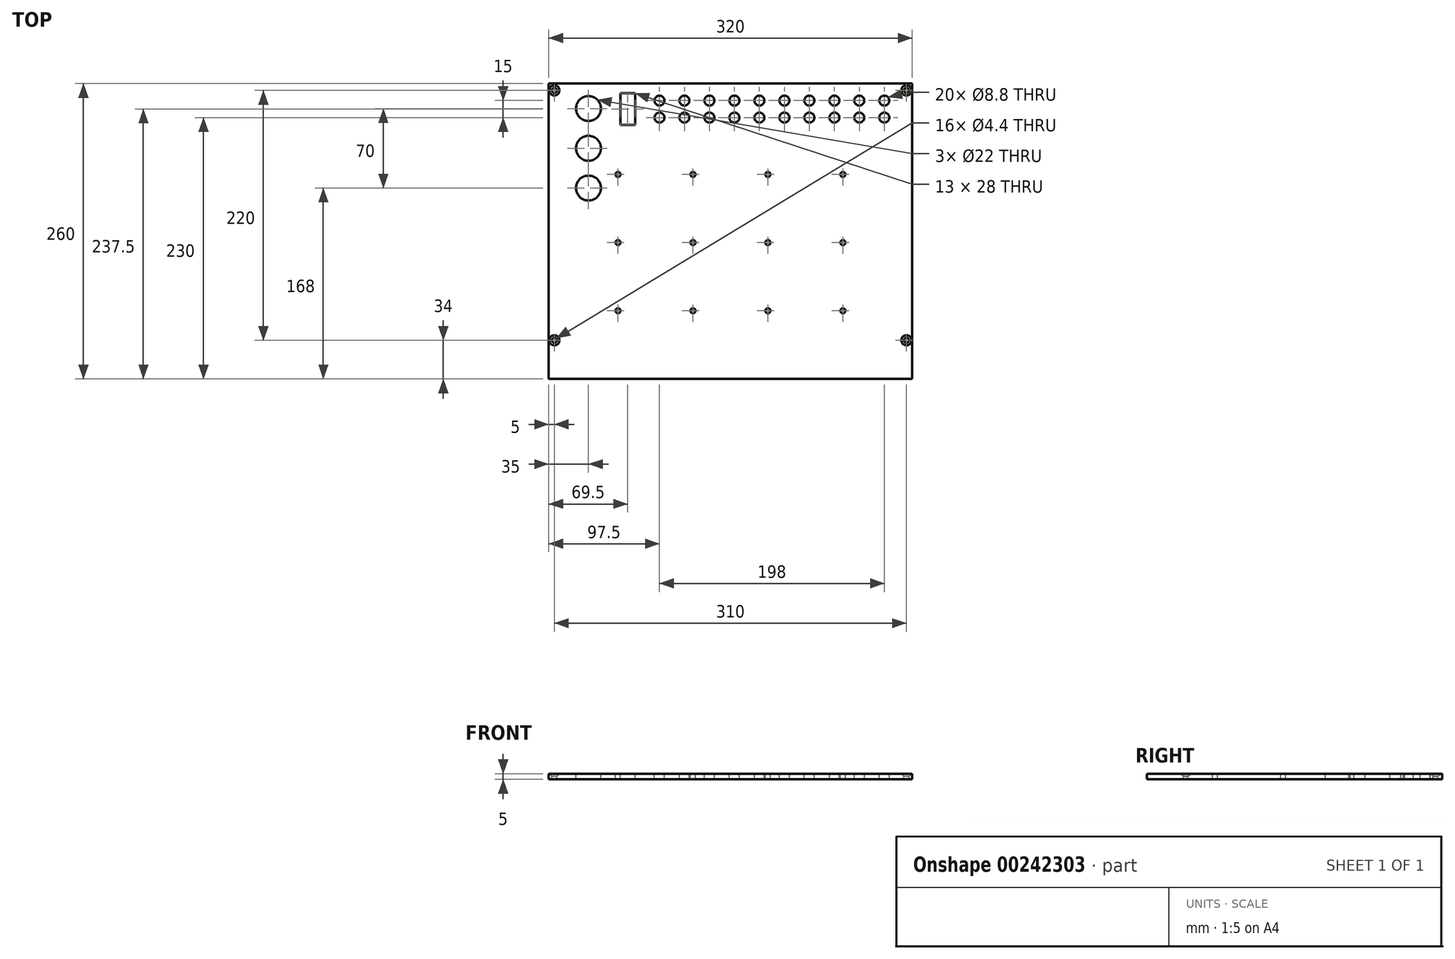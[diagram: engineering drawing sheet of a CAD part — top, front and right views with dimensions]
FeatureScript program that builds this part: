
annotation { "Feature Type Name" : "Feature", "Feature Type Description" : "" }
export const myFeature = defineFeature(function(context is Context, id is Id, definition is map)
    precondition{}
    {
        {
            var Q0;
            Q0=qCreatedBy(makeId("Top.planeOp"),FACE);
            var sketch = newSketch(context, id + "F0", { "sketchPlane" : qUnion([Q0])});
            skLineSegment(sketch, "E0.bottom", {"start": v(160, -130) * mm, "end": v(-160, -130) * mm});
            skLineSegment(sketch, "E0.top", {"start": v(160, 130) * mm, "end": v(-160, 130) * mm});
            skLineSegment(sketch, "E0.left", {"start": v(160, -130) * mm, "end": v(160, 130) * mm});
            skLineSegment(sketch, "E0.right", {"start": v(-160, -130) * mm, "end": v(-160, 130) * mm});
            skPoint(sketch, "E0.middle", {"position": v(0, 0) * mm});
            skSolve(sketch);
        }
        {
            var Q0;
            Q0=qSketchRegion(id+"F0",true);
            extrude(context, id + "F1", {"entities" : qUnion([Q0]), "endBound" : BoundingType.SYMMETRIC, "depth" : 5 * mm});
        }
        {
            var Q0;
            Q0=makeQuery(id+"F1.opExtrude","CAP_FACE",FACE,{"disambiguationData":[OSD([sQuery(id+"F0.wireOp",EDGE,"E0.bottom"),sQuery(id+"F0.wireOp",EDGE,"E0.top"),sQuery(id+"F0.wireOp",EDGE,"E0.left"),sQuery(id+"F0.wireOp",EDGE,"E0.right")])],"isStart":false});
            var sketch = newSketch(context, id + "F2", { "sketchPlane" : qUnion([Q0])});
            skCircle(sketch, "E1", {"center": v(-155, -96) * mm, "radius": 2 * mm});
            skCircle(sketch, "E2.0.1.0", {"center": v(-155, 124) * mm, "radius": 2 * mm});
            skCircle(sketch, "E2.1.0.0", {"center": v(155, -96) * mm, "radius": 2 * mm});
            skCircle(sketch, "E2.1.1.0", {"center": v(155, 124) * mm, "radius": 2 * mm});
            skLineSegment(sketch, "E2.direction1", {"start": v(-155, -96) * mm, "end": v(155, -96) * mm, "construction": true});
            skLineSegment(sketch, "E2.direction2", {"start": v(-155, -96) * mm, "end": v(-155, 124) * mm, "construction": true});
            skSolve(sketch);
        }
        {
            var Q0;
            Q0=sQuery(id+"F2.wireOp",VERTEX,"E1.center");
            var Q1;
            Q1=sQuery(id+"F2.wireOp",VERTEX,"E2.0.1.0.center");
            var Q2;
            Q2=sQuery(id+"F2.wireOp",VERTEX,"E2.1.1.0.center");
            var Q3;
            Q3=sQuery(id+"F2.wireOp",VERTEX,"E2.1.0.0.center");
            var Q4;
            Q4=makeQuery(id+"F1.opExtrude","SWEPT_BODY",BODY,{"disambiguationData":[OSD([sQuery(id+"F0.wireOp",EDGE,"E0.bottom"),sQuery(id+"F0.wireOp",EDGE,"E0.top"),sQuery(id+"F0.wireOp",EDGE,"E0.left"),sQuery(id+"F0.wireOp",EDGE,"E0.right")])]});
            hole(context, id + "F3", {"style" : HoleStyle.C_SINK, "endStyle" : HoleEndStyle.BLIND, "standardTappedOrClearance" : lookupTablePath({ "standard" : "ISO", "fit" : "Normal", "size" : "M4", "type" : "Clearance" }), "standardBlindInLast" : lookupTablePath({ "fit" : "Standard", "standard" : "ISO", "size" : "M4", "type" : "Clearance" }), "holeDiameter" : 4.4 * mm, "cSinkDiameter" : 8.96 * mm, "cSinkAngle" : 90 * degree, "holeDepth" : 17.25 * mm, "tappedDepth" : 15 * mm, "tapClearance" : 3, "locations" : qUnion([Q0, Q1, Q2, Q3]), "scope" : qUnion([Q4])});
        }
        {
            var Q0;
            Q0=makeQuery(id+"F1.opExtrude","CAP_FACE",FACE,{"disambiguationData":[OSD([sQuery(id+"F0.wireOp",EDGE,"E0.bottom"),sQuery(id+"F0.wireOp",EDGE,"E0.top"),sQuery(id+"F0.wireOp",EDGE,"E0.left"),sQuery(id+"F0.wireOp",EDGE,"E0.right")])],"isStart":false});
            var sketch = newSketch(context, id + "F4", { "sketchPlane" : qUnion([Q0])});
            skCircle(sketch, "E3", {"center": v(-62.5, 115) * mm, "radius": 4 * mm});
            skCircle(sketch, "E4.0.1.0", {"center": v(-62.5, 100) * mm, "radius": 4 * mm});
            skCircle(sketch, "E4.1.0.0", {"center": v(-40.5, 115) * mm, "radius": 4 * mm});
            skCircle(sketch, "E4.1.1.0", {"center": v(-40.5, 100) * mm, "radius": 4 * mm});
            skCircle(sketch, "E4.2.0.0", {"center": v(-18.5, 115) * mm, "radius": 4 * mm});
            skCircle(sketch, "E4.2.1.0", {"center": v(-18.5, 100) * mm, "radius": 4 * mm});
            skCircle(sketch, "E4.3.0.0", {"center": v(3.5, 115) * mm, "radius": 4 * mm});
            skCircle(sketch, "E4.3.1.0", {"center": v(3.5, 100) * mm, "radius": 4 * mm});
            skCircle(sketch, "E4.4.0.0", {"center": v(25.5, 115) * mm, "radius": 4 * mm});
            skCircle(sketch, "E4.4.1.0", {"center": v(25.5, 100) * mm, "radius": 4 * mm});
            skCircle(sketch, "E4.5.0.0", {"center": v(47.5, 115) * mm, "radius": 4 * mm});
            skCircle(sketch, "E4.5.1.0", {"center": v(47.5, 100) * mm, "radius": 4 * mm});
            skCircle(sketch, "E4.6.0.0", {"center": v(69.5, 115) * mm, "radius": 4 * mm});
            skCircle(sketch, "E4.6.1.0", {"center": v(69.5, 100) * mm, "radius": 4 * mm});
            skCircle(sketch, "E4.7.0.0", {"center": v(91.5, 115) * mm, "radius": 4 * mm});
            skCircle(sketch, "E4.7.1.0", {"center": v(91.5, 100) * mm, "radius": 4 * mm});
            skCircle(sketch, "E4.8.0.0", {"center": v(113.5, 115) * mm, "radius": 4 * mm});
            skCircle(sketch, "E4.8.1.0", {"center": v(113.5, 100) * mm, "radius": 4 * mm});
            skLineSegment(sketch, "E4.direction1", {"start": v(-62.5, 115) * mm, "end": v(-40.5, 115) * mm, "construction": true});
            skLineSegment(sketch, "E4.direction2", {"start": v(-62.5, 115) * mm, "end": v(-62.5, 100) * mm, "construction": true});
            skCircle(sketch, "E5.0.9.0", {"center": v(135.5, 115) * mm, "radius": 4 * mm});
            skCircle(sketch, "E5.0.9.1", {"center": v(135.5, 100) * mm, "radius": 4 * mm});
            skSolve(sketch);
        }
        {
            var Q0;
            Q0=sQuery(id+"F4.wireOp",VERTEX,"E3.center");
            var Q1;
            Q1=sQuery(id+"F4.wireOp",VERTEX,"E4.0.1.0.center");
            var Q2;
            Q2=sQuery(id+"F4.wireOp",VERTEX,"E4.1.0.0.center");
            var Q3;
            Q3=sQuery(id+"F4.wireOp",VERTEX,"E4.1.1.0.center");
            var Q4;
            Q4=sQuery(id+"F4.wireOp",VERTEX,"E4.2.0.0.center");
            var Q5;
            Q5=sQuery(id+"F4.wireOp",VERTEX,"E4.3.1.0.center");
            var Q6;
            Q6=sQuery(id+"F4.wireOp",VERTEX,"E4.3.0.0.center");
            var Q7;
            Q7=sQuery(id+"F4.wireOp",VERTEX,"E4.2.1.0.center");
            var Q8;
            Q8=sQuery(id+"F4.wireOp",VERTEX,"E4.4.1.0.center");
            var Q9;
            Q9=sQuery(id+"F4.wireOp",VERTEX,"E4.4.0.0.center");
            var Q10;
            Q10=sQuery(id+"F4.wireOp",VERTEX,"E4.5.0.0.center");
            var Q11;
            Q11=sQuery(id+"F4.wireOp",VERTEX,"E4.6.0.0.center");
            var Q12;
            Q12=sQuery(id+"F4.wireOp",VERTEX,"E4.7.0.0.center");
            var Q13;
            Q13=sQuery(id+"F4.wireOp",VERTEX,"E4.7.1.0.center");
            var Q14;
            Q14=sQuery(id+"F4.wireOp",VERTEX,"E4.8.1.0.center");
            var Q15;
            Q15=sQuery(id+"F4.wireOp",VERTEX,"E4.8.0.0.center");
            var Q16;
            Q16=sQuery(id+"F4.wireOp",VERTEX,"E4.9.0.0.center");
            var Q17;
            Q17=sQuery(id+"F4.wireOp",VERTEX,"E4.9.1.0.center");
            var Q18;
            Q18=sQuery(id+"F4.wireOp",VERTEX,"E4.10.0.0.center");
            var Q19;
            Q19=sQuery(id+"F4.wireOp",VERTEX,"E4.10.1.0.center");
            var Q20;
            Q20=sQuery(id+"F4.wireOp",VERTEX,"E4.11.0.0.center");
            var Q21;
            Q21=sQuery(id+"F4.wireOp",VERTEX,"E4.5.1.0.center");
            var Q22;
            Q22=sQuery(id+"F4.wireOp",VERTEX,"E4.6.1.0.center");
            var Q23;
            Q23=sQuery(id+"F4.wireOp",VERTEX,"E4.11.1.0.center");
            var Q24;
            Q24=sQuery(id+"F4.wireOp",VERTEX,"E5.0.9.0.center");
            var Q25;
            Q25=sQuery(id+"F4.wireOp",VERTEX,"E5.0.9.1.center");
            var Q26;
            Q26=makeQuery(id+"F1.opExtrude","SWEPT_BODY",BODY,{"disambiguationData":[OSD([sQuery(id+"F0.wireOp",EDGE,"E0.bottom"),sQuery(id+"F0.wireOp",EDGE,"E0.top"),sQuery(id+"F0.wireOp",EDGE,"E0.left"),sQuery(id+"F0.wireOp",EDGE,"E0.right")])]});
            hole(context, id + "F5", {"style" : HoleStyle.SIMPLE, "endStyle" : HoleEndStyle.BLIND, "standardTappedOrClearance" : lookupTablePath({ "standard" : "ISO", "fit" : "Normal", "size" : "M8", "type" : "Clearance" }), "standardBlindInLast" : lookupTablePath({ "fit" : "Standard", "standard" : "ISO", "size" : "M8", "type" : "Clearance" }), "holeDiameter" : 8.8 * mm, "holeDepth" : 17.25 * mm, "tappedDepth" : 15 * mm, "tapClearance" : 3, "locations" : qUnion([Q0, Q1, Q2, Q3, Q4, Q5, Q6, Q7, Q8, Q9, Q10, Q11, Q12, Q13, Q14, Q15, Q16, Q17, Q18, Q19, Q20, Q21, Q22, Q23, Q24, Q25]), "scope" : qUnion([Q26])});
        }
        {
            var Q0;
            Q0=makeQuery(id+"F1.opExtrude","CAP_FACE",FACE,{"disambiguationData":[OSD([sQuery(id+"F0.wireOp",EDGE,"E0.bottom"),sQuery(id+"F0.wireOp",EDGE,"E0.top"),sQuery(id+"F0.wireOp",EDGE,"E0.left"),sQuery(id+"F0.wireOp",EDGE,"E0.right")])],"isStart":false});
            var sketch = newSketch(context, id + "F6", { "sketchPlane" : qUnion([Q0])});
            skCircle(sketch, "E6", {"center": v(-99, -70) * mm, "radius": 2.5 * mm});
            skCircle(sketch, "E7.0.1.0", {"center": v(-99, -10) * mm, "radius": 2.5 * mm});
            skCircle(sketch, "E7.0.2.0", {"center": v(-99, 50) * mm, "radius": 2.5 * mm});
            skCircle(sketch, "E7.1.0.0", {"center": v(-33, -70) * mm, "radius": 2.5 * mm});
            skCircle(sketch, "E7.1.1.0", {"center": v(-33, -10) * mm, "radius": 2.5 * mm});
            skCircle(sketch, "E7.1.2.0", {"center": v(-33, 50) * mm, "radius": 2.5 * mm});
            skCircle(sketch, "E7.2.0.0", {"center": v(33, -70) * mm, "radius": 2.5 * mm});
            skCircle(sketch, "E7.2.1.0", {"center": v(33, -10) * mm, "radius": 2.5 * mm});
            skCircle(sketch, "E7.2.2.0", {"center": v(33, 50) * mm, "radius": 2.5 * mm});
            skCircle(sketch, "E7.3.0.0", {"center": v(99, -70) * mm, "radius": 2.5 * mm});
            skCircle(sketch, "E7.3.1.0", {"center": v(99, -10) * mm, "radius": 2.5 * mm});
            skCircle(sketch, "E7.3.2.0", {"center": v(99, 50) * mm, "radius": 2.5 * mm});
            skLineSegment(sketch, "E7.direction1", {"start": v(-99, -70) * mm, "end": v(-33, -70) * mm, "construction": true});
            skLineSegment(sketch, "E7.direction2", {"start": v(-99, -70) * mm, "end": v(-99, -10) * mm, "construction": true});
            skSolve(sketch);
        }
        {
            var Q0;
            Q0=sQuery(id+"F6.wireOp",VERTEX,"E7.0.2.0.center");
            var Q1;
            Q1=sQuery(id+"F6.wireOp",VERTEX,"E7.0.1.0.center");
            var Q2;
            Q2=sQuery(id+"F6.wireOp",VERTEX,"E6.center");
            var Q3;
            Q3=sQuery(id+"F6.wireOp",VERTEX,"E7.direction1.end");
            var Q4;
            Q4=sQuery(id+"F6.wireOp",VERTEX,"E7.1.1.0.center");
            var Q5;
            Q5=sQuery(id+"F6.wireOp",VERTEX,"E7.1.2.0.center");
            var Q6;
            Q6=sQuery(id+"F6.wireOp",VERTEX,"E7.2.2.0.center");
            var Q7;
            Q7=sQuery(id+"F6.wireOp",VERTEX,"E7.3.2.0.center");
            var Q8;
            Q8=sQuery(id+"F6.wireOp",VERTEX,"E7.3.1.0.center");
            var Q9;
            Q9=sQuery(id+"F6.wireOp",VERTEX,"E7.2.1.0.center");
            var Q10;
            Q10=sQuery(id+"F6.wireOp",VERTEX,"E7.2.0.0.center");
            var Q11;
            Q11=sQuery(id+"F6.wireOp",VERTEX,"E7.3.0.0.center");
            var Q12;
            Q12=makeQuery(id+"F1.opExtrude","SWEPT_BODY",BODY,{"disambiguationData":[OSD([sQuery(id+"F0.wireOp",EDGE,"E0.bottom"),sQuery(id+"F0.wireOp",EDGE,"E0.top"),sQuery(id+"F0.wireOp",EDGE,"E0.left"),sQuery(id+"F0.wireOp",EDGE,"E0.right")])]});
            hole(context, id + "F7", {"style" : HoleStyle.SIMPLE, "endStyle" : HoleEndStyle.BLIND, "standardTappedOrClearance" : lookupTablePath({ "standard" : "ISO", "fit" : "Normal", "size" : "M4", "type" : "Clearance" }), "standardBlindInLast" : lookupTablePath({ "fit" : "Standard", "standard" : "ISO", "size" : "M4", "type" : "Clearance" }), "holeDiameter" : 4.4 * mm, "holeDepth" : 17.25 * mm, "tappedDepth" : 15 * mm, "tapClearance" : 3, "locations" : qUnion([Q0, Q1, Q2, Q3, Q4, Q5, Q6, Q7, Q8, Q9, Q10, Q11]), "scope" : qUnion([Q12])});
        }
        {
            var Q0;
            Q0=makeQuery(id+"F1.opExtrude","CAP_FACE",FACE,{"disambiguationData":[OSD([sQuery(id+"F0.wireOp",EDGE,"E0.bottom"),sQuery(id+"F0.wireOp",EDGE,"E0.top"),sQuery(id+"F0.wireOp",EDGE,"E0.left"),sQuery(id+"F0.wireOp",EDGE,"E0.right")])],"isStart":false});
            var sketch = newSketch(context, id + "F8", { "sketchPlane" : qUnion([Q0])});
            skCircle(sketch, "E8", {"center": v(-125, 108) * mm, "radius": 11 * mm});
            skCircle(sketch, "E9.0.1.0", {"center": v(-125, 73) * mm, "radius": 11 * mm});
            skCircle(sketch, "E9.0.2.0", {"center": v(-125, 38) * mm, "radius": 11 * mm});
            skLineSegment(sketch, "E9.direction1", {"start": v(-125, 108) * mm, "end": v(-114, 108) * mm, "construction": true});
            skLineSegment(sketch, "E9.direction2", {"start": v(-125, 108) * mm, "end": v(-125, 73) * mm, "construction": true});
            skSolve(sketch);
        }
        {
            var Q0;
            Q0=sQuery(id+"F8.wireOp",VERTEX,"E9.direction1.start");
            var Q1;
            Q1=sQuery(id+"F8.wireOp",VERTEX,"E9.0.1.0.center");
            var Q2;
            Q2=sQuery(id+"F8.wireOp",VERTEX,"E9.0.2.0.center");
            var Q3;
            Q3=makeQuery(id+"F1.opExtrude","SWEPT_BODY",BODY,{"disambiguationData":[OSD([sQuery(id+"F0.wireOp",EDGE,"E0.bottom"),sQuery(id+"F0.wireOp",EDGE,"E0.top"),sQuery(id+"F0.wireOp",EDGE,"E0.left"),sQuery(id+"F0.wireOp",EDGE,"E0.right")])]});
            hole(context, id + "F9", {"style" : HoleStyle.SIMPLE, "endStyle" : HoleEndStyle.BLIND, "holeDiameter" : 22 * mm, "holeDepth" : 17.25 * mm, "tappedDepth" : 15 * mm, "tapClearance" : 3, "locations" : qUnion([Q0, Q1, Q2]), "scope" : qUnion([Q3])});
        }
        {
            var Q0;
            Q0=makeQuery(id+"F8.imprint","IMPRINT",FACE,{"disambiguationData":[TD([[makeQuery(id+"F8.imprint","IMPRINT",EDGE,{"derivedFrom":sQuery(id+"F8.wireOp",EDGE,"E8")}),-1.0]])]});
            var sketch = newSketch(context, id + "F10", { "sketchPlane" : qUnion([Q0])});
            skLineSegment(sketch, "E10.bottom", {"start": v(-84, 93.5) * mm, "end": v(-97, 93.5) * mm});
            skLineSegment(sketch, "E10.top", {"start": v(-84, 121.5) * mm, "end": v(-97, 121.5) * mm});
            skLineSegment(sketch, "E10.left", {"start": v(-84, 93.5) * mm, "end": v(-84, 121.5) * mm});
            skLineSegment(sketch, "E10.right", {"start": v(-97, 93.5) * mm, "end": v(-97, 121.5) * mm});
            skPoint(sketch, "E10.middle", {"position": v(-90.5, 107.5) * mm});
            skSolve(sketch);
        }
        {
            var Q0;
            Q0=makeQuery(id+"F10.imprint","IMPRINT",FACE,{"disambiguationData":[TD([[makeQuery(id+"F10.imprint","IMPRINT",EDGE,{"derivedFrom":sQuery(id+"F10.wireOp",EDGE,"E10.bottom")}),-1.0]])]});
            extrude(context, id + "F11", {"entities" : qUnion([Q0]), "operationType" : NewBodyOperationType.REMOVE, "oppositeDirection" : true, "depth" : 25 * mm});
        }
    });
